# Revit family: Wall_Shelves-Teknion-CWOH_Open-R2021
name_source: partatom
category: Furniture
units: mm (PartAtom-declared; Revit-internal decimal feet)

## family parameters
Always vertical = Yes
Cut with Voids When Loaded = No
OmniClass Number = 23.40.20.00
OmniClass Title = General Furniture and Specialties
Room Calculation Point = No
Shared = Yes
Work Plane-Based = No

## types (2) — shared parameters
Assembly Code = E2020200
Depth = 15 "
Manufacturer = Teknion
Manufacturer Fax = 416.661.4586
Part Number = CWOH
Product Documentation Link = https://www.teknion.com
Product Line = Chronicle
Product Page URL = https://www.teknion.com
Series = Chronicle
Sustainability Data = https://www.teknion.com
URL = www.teknion.com
Unit Weight URL = http://www.teknion.com
Warranty = http://www.teknion.com
zero-valued in all types: Default Elevation

## per-type parameters (varying)
| type | Description | Height | Model |
| (3H) 3 High,41.25" | Open Wall Shelves, (3H) 3 High - 41.25" | 41.25 " | CWOH3H15____ |
| (4H) 4 high, 55" | Open Wall Shelves, (4H) 4 High - 55" | 55 " | CWOH4H15____ |

## geometry (parser evidence)
native form markers: Sweep x3
no freeform markers — native parametric forms only
